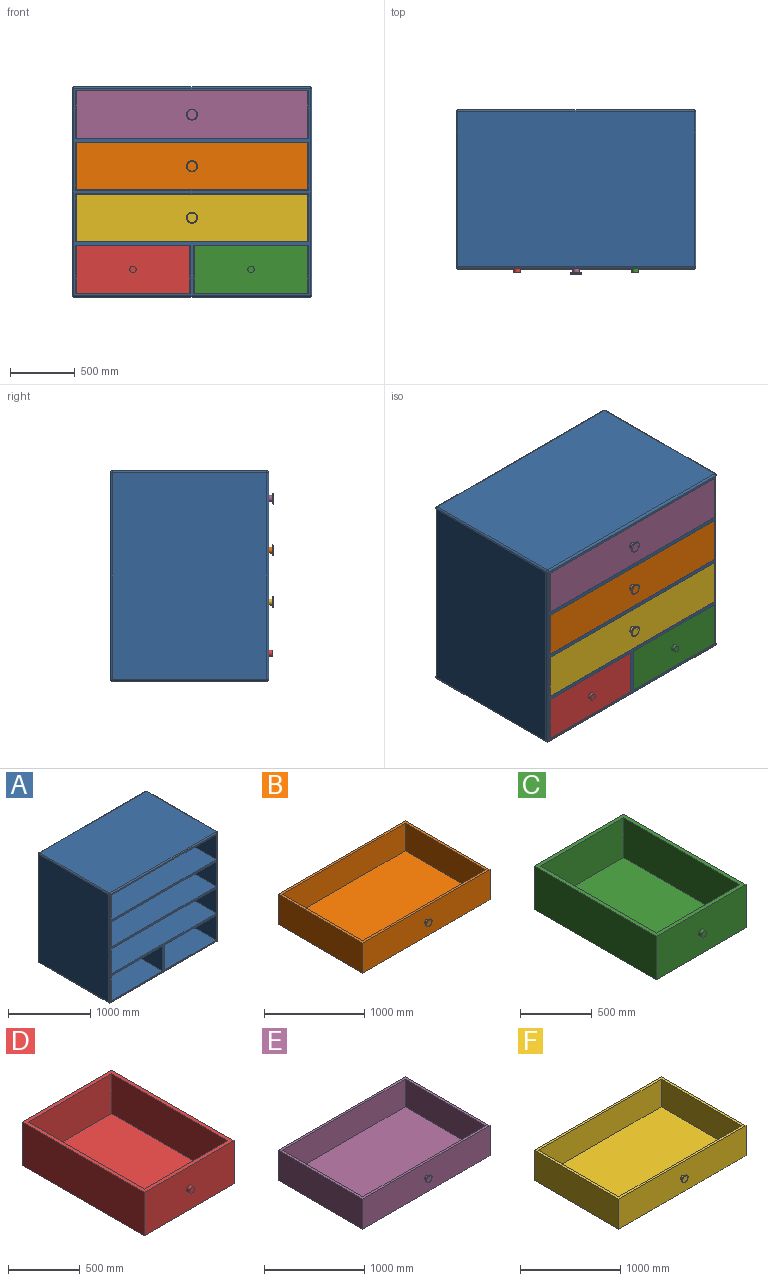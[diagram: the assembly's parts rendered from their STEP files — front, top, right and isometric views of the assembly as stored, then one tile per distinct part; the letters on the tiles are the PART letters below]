
ASSEMBLY  parts=6 mates=5
PART A: 51 faces, bbox 1860x1230x1630 mm
  f0: plane 885x370mm, normal (0,-1,0), area 327450mm2, adj f15,f21,f28,f29
  f1: plane 1200x885mm, normal (0,0,1), area 1062000mm2, adj f3,f12,f20,f30
  f2: plane 1200x885mm, normal (0,0,-1), area 1062000mm2, adj f3,f12,f20,f30
  f3: plane 1200x370mm, normal (-1,0,0), area 444000mm2, adj f1,f2,f12,f20
  f4: plane 1200x370mm, normal (1,0,0), area 444000mm2, adj f5,f12,f23,f27
  f5: plane 1800x370mm, normal (0,-1,0), area 666000mm2, adj f4,f10,f23,f27
  f6: plane 1200x370mm, normal (1,0,0), area 444000mm2, adj f7,f12,f14,f25
  f7: plane 1800x370mm, normal (0,-1,0), area 666000mm2, adj f6,f14,f17,f25
  f8: plane 1200x370mm, normal (-1,0,0), area 444000mm2, adj f11,f12,f24,f26
  f9: plane 1200x370mm, normal (1,0,0), area 444000mm2, adj f11,f12,f24,f26
  f10: plane 1200x370mm, normal (-1,0,0), area 444000mm2, adj f5,f12,f23,f27
  f11: plane 1800x370mm, normal (0,-1,0), area 666000mm2, adj f8,f9,f24,f26
  f12: plane 1830x1600mm, normal (0,-1,0), area 275100mm2, adj f1,f2,f3,f4,f6,f8,f9,f10
  f13: plane 1830x1200mm, normal (0,0,1), area 2196000mm2, adj f31,f35,f36,f37
  f14: plane 1800x1200mm, normal (0,0,-1), area 2160000mm2, adj f6,f7,f12,f17
  f15: plane 1200x370mm, normal (1,0,0), area 444000mm2, adj f0,f12,f21,f28
  f16: plane 1600x1200mm, normal (-1,0,0), area 1920000mm2, adj f37,f38,f46,f47
  f17: plane 1200x370mm, normal (-1,0,0), area 444000mm2, adj f7,f12,f14,f25
  f18: plane 1600x1200mm, normal (1,0,0), area 1920000mm2, adj f34,f35,f44,f45
  f19: plane 1830x1600mm, normal (0,1,0), area 2928000mm2, adj f36,f45,f46,f50
  f20: plane 885x370mm, normal (0,-1,0), area 327450mm2, adj f1,f2,f3,f30
  f21: plane 1200x885mm, normal (0,0,1), area 1062000mm2, adj f0,f12,f15,f29
  f22: plane 1830x1200mm, normal (0,0,-1), area 2196000mm2, adj f39,f44,f47,f50
  f23: plane 1800x1200mm, normal (0,0,-1), area 2160000mm2, adj f4,f5,f10,f12
  f24: plane 1800x1200mm, normal (0,0,1), area 2160000mm2, adj f8,f9,f11,f12
  f25: plane 1800x1200mm, normal (0,0,1), area 2160000mm2, adj f6,f7,f12,f17
  f26: plane 1800x1200mm, normal (0,0,-1), area 2160000mm2, adj f8,f9,f11,f12
  f27: plane 1800x1200mm, normal (0,0,1), area 2160000mm2, adj f4,f5,f10,f12
  f28: plane 1200x885mm, normal (0,0,-1), area 1062000mm2, adj f0,f12,f15,f29
  f29: plane 1200x370mm, normal (-1,0,0), area 444000mm2, adj f0,f12,f21,f28
  f30: plane 1200x370mm, normal (1,0,0), area 444000mm2, adj f1,f2,f12,f20
  f31: cylinder r=15mm len=1830mm, axis (-1,0,0), area 43118.4mm2, adj f12,f13,f32,f33
  f32: sphere r=15mm, area 353.4mm2, adj f31,f34,f35
  f33: sphere r=15mm, area 353.4mm2, adj f31,f37,f38
  f34: cylinder r=15mm len=1600mm, axis (0,0,-1), area 37699.1mm2, adj f12,f18,f32,f40
  f35: cylinder r=15mm len=1200mm, axis (0,-1,0), area 28274.3mm2, adj f13,f18,f32,f41
  f36: cylinder r=15mm len=1830mm, axis (-1,0,0), area 43118.4mm2, adj f13,f19,f41,f42
  f37: cylinder r=15mm len=1200mm, axis (0,-1,0), area 28274.3mm2, adj f13,f16,f33,f42
  f38: cylinder r=15mm len=1600mm, axis (0,0,-1), area 37699.1mm2, adj f12,f16,f33,f43
  f39: cylinder r=15mm len=1830mm, axis (1,0,0), area 43118.4mm2, adj f12,f22,f40,f43
  f40: sphere r=15mm, area 353.4mm2, adj f34,f39,f44
  f41: sphere r=15mm, area 353.4mm2, adj f35,f36,f45
  f42: sphere r=15mm, area 353.4mm2, adj f36,f37,f46
  f43: sphere r=15mm, area 353.4mm2, adj f38,f39,f47
  f44: cylinder r=15mm len=1200mm, axis (0,-1,0), area 28274.3mm2, adj f18,f22,f40,f48
  f45: cylinder r=15mm len=1600mm, axis (0,0,-1), area 37699.1mm2, adj f18,f19,f41,f48
  f46: cylinder r=15mm len=1600mm, axis (0,0,-1), area 37699.1mm2, adj f16,f19,f42,f49
  f47: cylinder r=15mm len=1200mm, axis (0,-1,0), area 28274.3mm2, adj f16,f22,f43,f49
  f48: sphere r=15mm, area 353.4mm2, adj f44,f45,f50
  f49: sphere r=15mm, area 353.4mm2, adj f46,f47,f50
  f50: cylinder r=15mm len=1830mm, axis (-1,0,0), area 43118.4mm2, adj f19,f22,f48,f49
PART B: 15 faces, bbox 1798x1240x368 mm
  f0: plane 1738x1140mm, normal (0,0,1), area 1981320mm2, adj f1,f2,f3,f10
  f1: plane 1140x338mm, normal (1,0,0), area 385320mm2, adj f0,f3,f5,f10
  f2: plane 1140x338mm, normal (-1,0,0), area 385320mm2, adj f0,f3,f5,f10
  f3: plane 1738x338mm, normal (0,-1,0), area 587444mm2, adj f0,f1,f2,f5
  f4: plane 1200x368mm, normal (1,0,0), area 441600mm2, adj f5,f7,f8,f9
  f5: plane 1798x1200mm, normal (0,0,1), area 176280mm2, adj f1,f2,f3,f4,f6,f8,f9,f10
  f6: plane 1200x368mm, normal (-1,0,0), area 441600mm2, adj f5,f7,f8,f9
  f7: plane 1798x1200mm, normal (0,0,-1), area 2157600mm2, adj f4,f6,f8,f9
  f8: plane 1798x368mm, normal (0,1,0), area 661664mm2, adj f4,f5,f6,f7
  f9: plane 1798x368mm, normal (0,-1,0), area 659700.5mm2, adj f4,f5,f6,f7,f11
  f10: plane 1738x338mm, normal (0,1,0), area 587444mm2, adj f0,f1,f2,f5
  f11: cylinder r=25mm len=50mm, axis (0,1,0), area 4712.4mm2, adj f9,f13
  f12: plane 75.11x75.11mm, normal (0,-1,0), area 4431.2mm2, adj f14
  f13: plane 75.11x75.11mm, normal (0,1,0), area 2467.7mm2, adj f11,f14
  f14: torus R=37.56mm, axis (0,-1,0), area 4020.8mm2, adj f12,f13
PART C: 13 faces, bbox 883x1230x368 mm
  f0: plane 1140x823mm, normal (0,0,1), area 938220mm2, adj f1,f8,f9,f10
  f1: plane 1140x338mm, normal (-1,0,0), area 385320mm2, adj f0,f7,f8,f10
  f2: plane 883x368mm, normal (0,-1,0), area 322980.5mm2, adj f3,f5,f6,f7,f11
  f3: plane 1200x368mm, normal (-1,0,0), area 441600mm2, adj f2,f4,f6,f7
  f4: plane 883x368mm, normal (0,1,0), area 324944mm2, adj f3,f5,f6,f7
  f5: plane 1200x368mm, normal (1,0,0), area 441600mm2, adj f2,f4,f6,f7
  f6: plane 1200x883mm, normal (0,0,-1), area 1059600mm2, adj f2,f3,f4,f5
  f7: plane 1200x883mm, normal (0,0,1), area 121380mm2, adj f1,f2,f3,f4,f5,f8,f9,f10
  f8: plane 823x338mm, normal (0,-1,0), area 278174mm2, adj f0,f1,f7,f9
  f9: plane 1140x338mm, normal (1,0,0), area 385320mm2, adj f0,f7,f8,f10
  f10: plane 823x338mm, normal (0,1,0), area 278174mm2, adj f0,f1,f7,f9
  f11: cylinder r=25mm len=50mm, axis (0,1,0), area 4712.4mm2, adj f2,f12
  f12: plane 50x50mm, normal (0,-1,0), area 1963.5mm2, adj f11
PART D: 13 faces, bbox 883x1230x368 mm
  f0: plane 1140x823mm, normal (0,0,1), area 938220mm2, adj f1,f8,f9,f10
  f1: plane 1140x338mm, normal (1,0,0), area 385320mm2, adj f0,f7,f8,f10
  f2: plane 883x368mm, normal (0,-1,0), area 322980.5mm2, adj f3,f5,f6,f7,f11
  f3: plane 1200x368mm, normal (1,0,0), area 441600mm2, adj f2,f4,f6,f7
  f4: plane 883x368mm, normal (0,1,0), area 324944mm2, adj f3,f5,f6,f7
  f5: plane 1200x368mm, normal (-1,0,0), area 441600mm2, adj f2,f4,f6,f7
  f6: plane 1200x883mm, normal (0,0,-1), area 1059600mm2, adj f2,f3,f4,f5
  f7: plane 1200x883mm, normal (0,0,1), area 121380mm2, adj f1,f2,f3,f4,f5,f8,f9,f10
  f8: plane 823x338mm, normal (0,-1,0), area 278174mm2, adj f0,f1,f7,f9
  f9: plane 1140x338mm, normal (-1,0,0), area 385320mm2, adj f0,f7,f8,f10
  f10: plane 823x338mm, normal (0,1,0), area 278174mm2, adj f0,f1,f7,f9
  f11: cylinder r=25mm len=50mm, axis (0,1,0), area 4712.4mm2, adj f2,f12
  f12: plane 50x50mm, normal (0,-1,0), area 1963.5mm2, adj f11
PART E: 15 faces, bbox 1798x1240x368 mm
  f0: plane 1738x1140mm, normal (0,0,1), area 1981320mm2, adj f1,f2,f3,f10
  f1: plane 1140x338mm, normal (1,0,0), area 385320mm2, adj f0,f3,f5,f10
  f2: plane 1140x338mm, normal (-1,0,0), area 385320mm2, adj f0,f3,f5,f10
  f3: plane 1738x338mm, normal (0,-1,0), area 587444mm2, adj f0,f1,f2,f5
  f4: plane 1200x368mm, normal (1,0,0), area 441600mm2, adj f5,f7,f8,f9
  f5: plane 1798x1200mm, normal (0,0,1), area 176280mm2, adj f1,f2,f3,f4,f6,f8,f9,f10
  f6: plane 1200x368mm, normal (-1,0,0), area 441600mm2, adj f5,f7,f8,f9
  f7: plane 1798x1200mm, normal (0,0,-1), area 2157600mm2, adj f4,f6,f8,f9
  f8: plane 1798x368mm, normal (0,1,0), area 661664mm2, adj f4,f5,f6,f7
  f9: plane 1798x368mm, normal (0,-1,0), area 659700.5mm2, adj f4,f5,f6,f7,f11
  f10: plane 1738x338mm, normal (0,1,0), area 587444mm2, adj f0,f1,f2,f5
  f11: cylinder r=25mm len=50mm, axis (0,1,0), area 4712.4mm2, adj f9,f13
  f12: plane 75.11x75.11mm, normal (0,-1,0), area 4431.2mm2, adj f14
  f13: plane 75.11x75.11mm, normal (0,1,0), area 2467.7mm2, adj f11,f14
  f14: torus R=37.56mm, axis (0,-1,0), area 4020.8mm2, adj f12,f13
PART F: 15 faces, bbox 1798x1240x368 mm
  f0: plane 1738x1140mm, normal (0,0,1), area 1981320mm2, adj f1,f2,f3,f10
  f1: plane 1140x338mm, normal (1,0,0), area 385320mm2, adj f0,f3,f5,f10
  f2: plane 1140x338mm, normal (-1,0,0), area 385320mm2, adj f0,f3,f5,f10
  f3: plane 1738x338mm, normal (0,-1,0), area 587444mm2, adj f0,f1,f2,f5
  f4: plane 1200x368mm, normal (1,0,0), area 441600mm2, adj f5,f7,f8,f9
  f5: plane 1798x1200mm, normal (0,0,1), area 176280mm2, adj f1,f2,f3,f4,f6,f8,f9,f10
  f6: plane 1200x368mm, normal (-1,0,0), area 441600mm2, adj f5,f7,f8,f9
  f7: plane 1798x1200mm, normal (0,0,-1), area 2157600mm2, adj f4,f6,f8,f9
  f8: plane 1798x368mm, normal (0,1,0), area 661664mm2, adj f4,f5,f6,f7
  f9: plane 1798x368mm, normal (0,-1,0), area 659700.5mm2, adj f4,f5,f6,f7,f11
  f10: plane 1738x338mm, normal (0,1,0), area 587444mm2, adj f0,f1,f2,f5
  f11: cylinder r=25mm len=50mm, axis (0,1,0), area 4712.4mm2, adj f9,f13
  f12: plane 75.11x75.11mm, normal (0,-1,0), area 4431.2mm2, adj f14
  f13: plane 75.11x75.11mm, normal (0,1,0), area 2467.7mm2, adj f11,f14
  f14: torus R=37.56mm, axis (0,-1,0), area 4020.8mm2, adj f12,f13
PLACE A t=(-578.78,0,418.87)mm fixed
PLACE B t=(-578.78,0,418.87)mm
PLACE C t=(-578.78,0,419.87)mm
PLACE D t=(-578.78,0,419.87)mm
PLACE E t=(-578.78,0,418.87)mm
PLACE F t=(-578.78,0,418.87)mm
MATE slider A.f0 <-> D.f11  axis (0,-1,0) through (-1036.28,600,-966.13)mm
MATE slider A.f5 <-> F.f11  axis (0,-1,0) through (-578.78,600,-566.13)mm
MATE slider A.f11 <-> B.f11  axis (0,-1,0) through (-578.78,600,-166.13)mm
MATE slider E.f11 <-> A.f7  axis (0,1,0) through (-578.78,600,233.87)mm
MATE slider A.f20 <-> C.f11  axis (0,-1,0) through (-121.28,600,-966.13)mm
